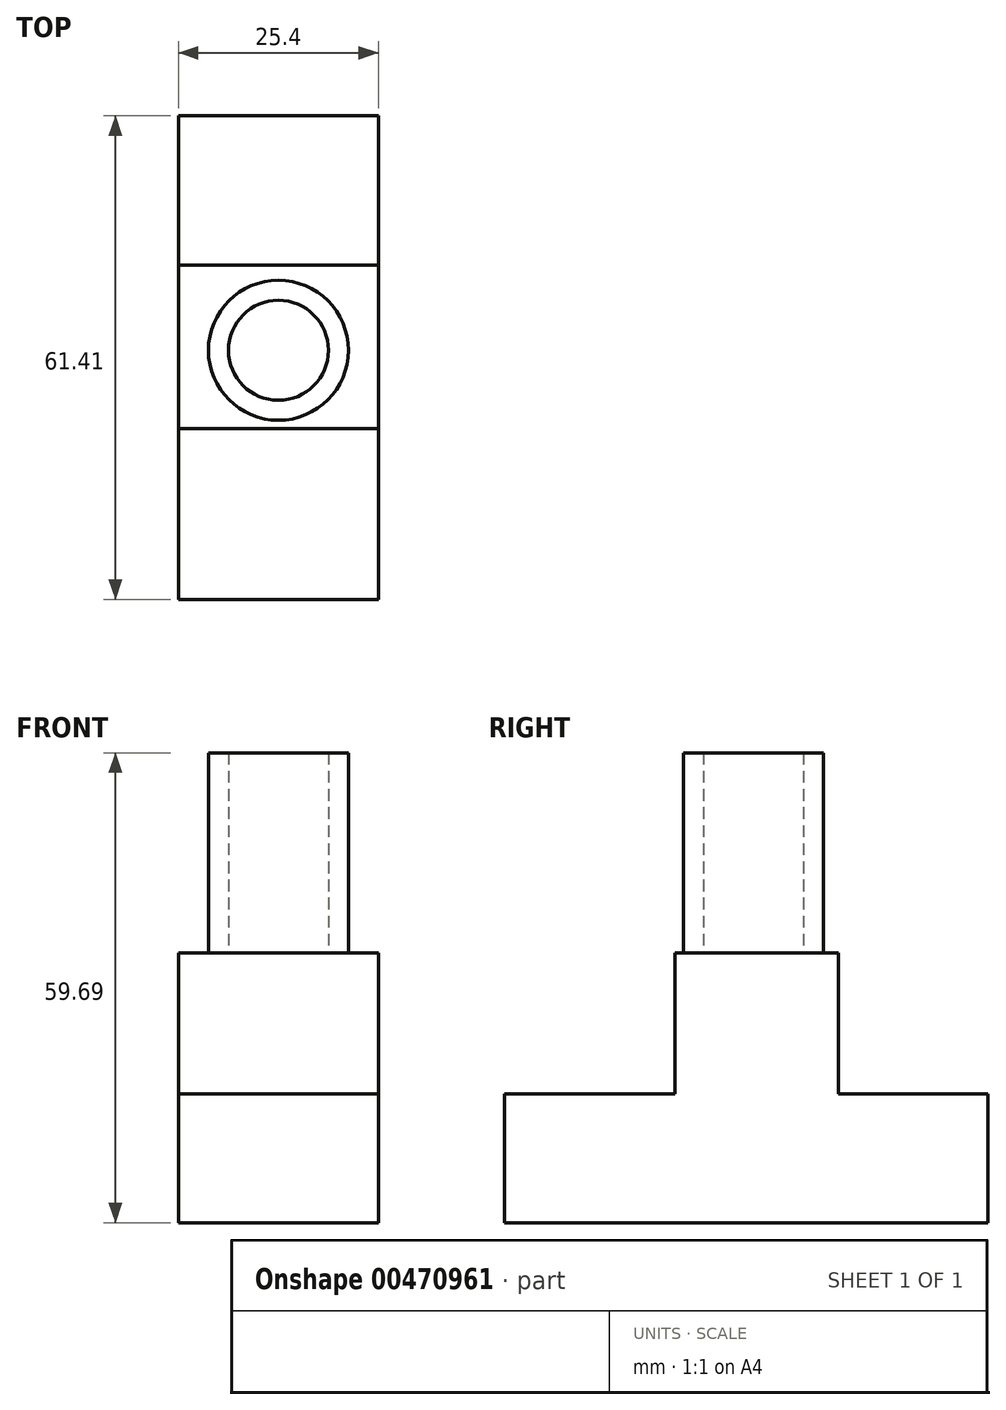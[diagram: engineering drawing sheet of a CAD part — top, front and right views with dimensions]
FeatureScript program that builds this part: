
annotation { "Feature Type Name" : "Feature", "Feature Type Description" : "" }
export const myFeature = defineFeature(function(context is Context, id is Id, definition is map)
    precondition{}
    {
        {
            var Q0;
            Q0=qCreatedBy(makeId("Right.planeOp"),FACE);
            var sketch = newSketch(context, id + "F0", { "sketchPlane" : qUnion([Q0])});
            skLineSegment(sketch, "E0", {"start": v(-31.63, 0) * mm, "end": v(-31.63, 16.34) * mm});
            skLineSegment(sketch, "E1", {"start": v(-31.63, 16.34) * mm, "end": v(-9.93, 16.34) * mm});
            skLineSegment(sketch, "E2", {"start": v(-9.93, 16.34) * mm, "end": v(-9.93, 34.3) * mm});
            skLineSegment(sketch, "E3", {"start": v(-9.93, 34.3) * mm, "end": v(10.83, 34.3) * mm});
            skLineSegment(sketch, "E4", {"start": v(10.83, 34.3) * mm, "end": v(10.83, 16.34) * mm});
            skLineSegment(sketch, "E5", {"start": v(10.83, 16.34) * mm, "end": v(29.78, 16.34) * mm});
            skLineSegment(sketch, "E6", {"start": v(29.78, 16.34) * mm, "end": v(29.78, 0) * mm});
            skLineSegment(sketch, "E7", {"start": v(29.78, 0) * mm, "end": v(0, 0) * mm});
            skLineSegment(sketch, "E8", {"start": v(-31.63, 0) * mm, "end": v(0, 0) * mm});
            skSolve(sketch);
        }
        {
            var Q0;
            Q0 = qSketchRegion(id + "F0", true);
            extrude(context, id + "F1", {"entities" : qUnion([Q0]), "depth" : 25.4 * mm});
        }
        {
            var Q0;
            Q0=makeQuery(id+"F1.opExtrude","SWEPT_FACE",FACE,{"disambiguationData":[OSD([sQuery(id+"F0.wireOp",EDGE,"E3")])]});
            var sketch = newSketch(context, id + "F2", { "sketchPlane" : qUnion([Q0])});
            skCircle(sketch, "E9", {"center": v(12.7, 0) * mm, "radius": 6.35 * mm});
            skCircle(sketch, "E10.0", {"center": v(12.7, 0) * mm, "radius": 8.9 * mm});
            skSolve(sketch);
        }
        {
            var Q0;
            Q0 = qSketchRegion(id + "F2", true);
            extrude(context, id + "F3", {"entities" : qUnion([Q0]), "operationType" : NewBodyOperationType.ADD, "depth" : 25.4 * mm});
        }
    });
